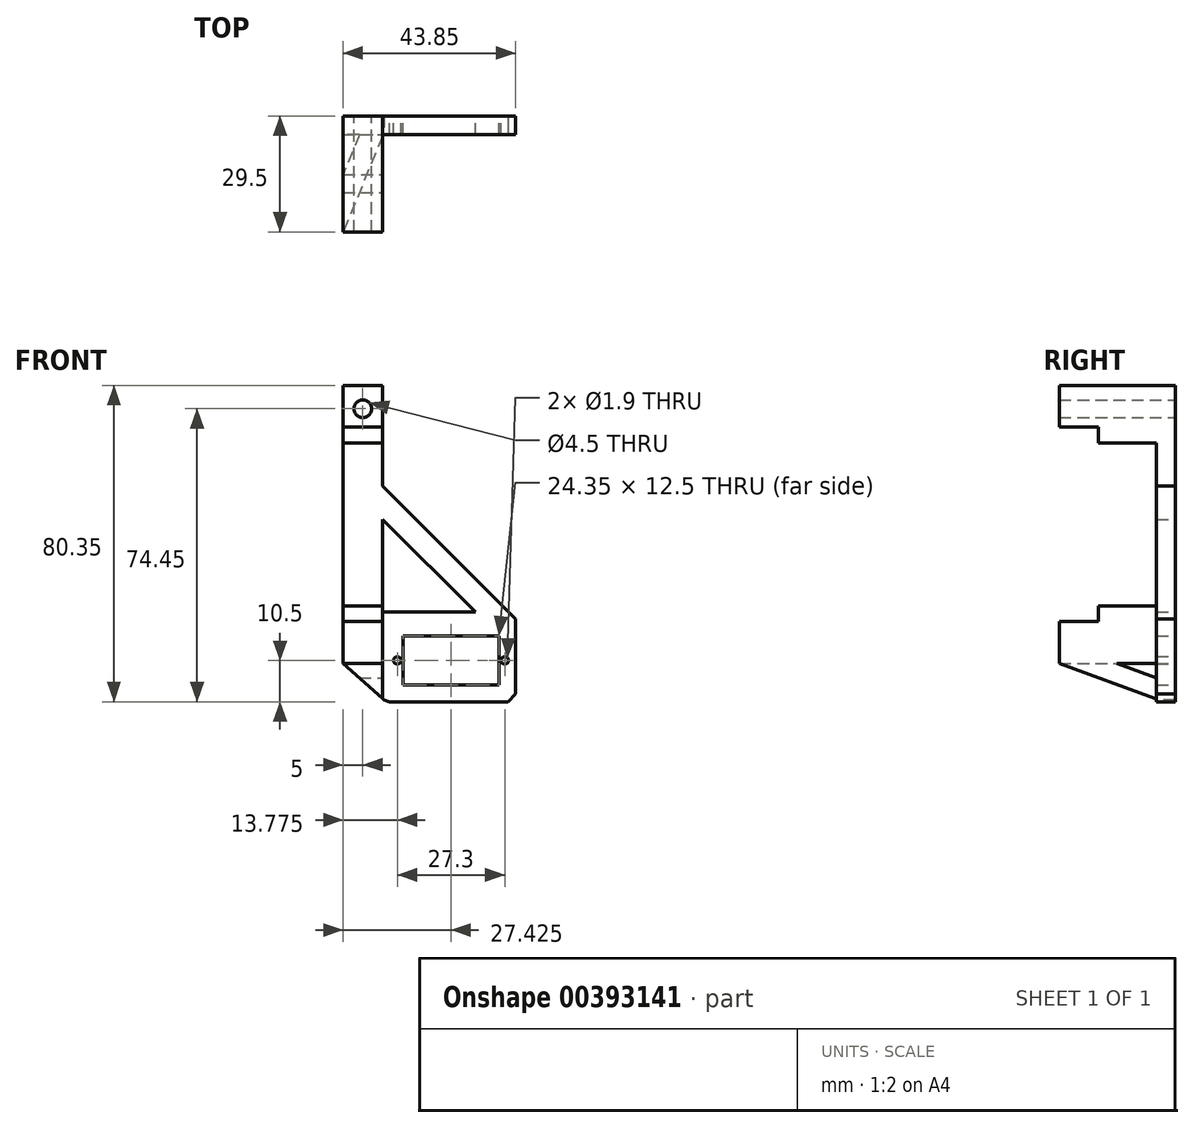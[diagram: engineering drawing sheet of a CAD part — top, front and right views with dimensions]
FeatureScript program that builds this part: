
annotation { "Feature Type Name" : "Feature", "Feature Type Description" : "" }
export const myFeature = defineFeature(function(context is Context, id is Id, definition is map)
    precondition{}
    {
        {
            var Q0;
            Q0=qCreatedBy(makeId("Front.planeOp"),FACE);
            var sketch = newSketch(context, id + "F0", { "sketchPlane" : qUnion([Q0])});
            skLineSegment(sketch, "E0", {"start": v(5, 35.3) * mm, "end": v(-5, 35.3) * mm});
            skPoint(sketch, "E1", {"position": v(0, 35.3) * mm});
            skLineSegment(sketch, "E2.MirrorCS", {"start": v(5, -35.3) * mm, "end": v(-5, -35.3) * mm});
            skPoint(sketch, "E3.MirrorP", {"position": v(0, -35.3) * mm});
            skLineSegment(sketch, "E4", {"start": v(-5, 35.3) * mm, "end": v(-5, -35.3) * mm});
            skLineSegment(sketch, "E5", {"start": v(5, -35.3) * mm, "end": v(5, 35.3) * mm});
            skLineSegment(sketch, "E6", {"start": v(-5, 24.7) * mm, "end": v(5, 24.7) * mm});
            skLineSegment(sketch, "E7", {"start": v(-5, 20.7) * mm, "end": v(5, 20.7) * mm});
            skLineSegment(sketch, "E8.MirrorCS", {"start": v(-5, -24.7) * mm, "end": v(5, -24.7) * mm});
            skLineSegment(sketch, "E9.MirrorCS", {"start": v(-5, -20.7) * mm, "end": v(5, -20.7) * mm});
            skCircle(sketch, "E10", {"center": v(0, 29.4) * mm, "radius": 2.25 * mm});
            skCircle(sketch, "E11.MirrorC", {"center": v(0, -29.4) * mm, "radius": 2.25 * mm});
            skLineSegment(sketch, "E12.bottom", {"start": v(10.25, -40.8) * mm, "end": v(34.6, -40.8) * mm});
            skLineSegment(sketch, "E12.top", {"start": v(10.25, -28.3) * mm, "end": v(34.6, -28.3) * mm});
            skLineSegment(sketch, "E12.left", {"start": v(10.25, -40.8) * mm, "end": v(10.25, -28.3) * mm});
            skLineSegment(sketch, "E12.right", {"start": v(34.6, -40.8) * mm, "end": v(34.6, -28.3) * mm});
            skPoint(sketch, "E12.middle", {"position": v(22.43, -34.55) * mm});
            skLineSegment(sketch, "E13.bottom", {"start": v(34.6, -28.3) * mm, "end": v(38.85, -28.3) * mm});
            skLineSegment(sketch, "E13.top", {"start": v(34.6, -40.8) * mm, "end": v(38.85, -40.8) * mm});
            skLineSegment(sketch, "E13.left", {"start": v(34.6, -28.3) * mm, "end": v(34.6, -40.8) * mm});
            skLineSegment(sketch, "E13.right", {"start": v(38.85, -28.3) * mm, "end": v(38.85, -40.8) * mm});
            skLineSegment(sketch, "E14.bottom", {"start": v(10.25, -28.3) * mm, "end": v(6, -28.3) * mm});
            skLineSegment(sketch, "E14.top", {"start": v(10.25, -40.8) * mm, "end": v(6, -40.8) * mm});
            skLineSegment(sketch, "E14.left", {"start": v(10.25, -28.3) * mm, "end": v(10.25, -40.8) * mm});
            skLineSegment(sketch, "E14.right", {"start": v(6, -28.3) * mm, "end": v(6, -40.8) * mm});
            skLineSegment(sketch, "E15.bottom", {"start": v(22.43, -28.3) * mm, "end": v(22.43, -28.3) * mm});
            skLineSegment(sketch, "E15.top", {"start": v(22.43, -40.8) * mm, "end": v(22.43, -40.8) * mm});
            skLineSegment(sketch, "E15.left", {"start": v(22.43, -28.3) * mm, "end": v(22.43, -40.8) * mm, "construction": true});
            skLineSegment(sketch, "E15.right", {"start": v(22.43, -28.3) * mm, "end": v(22.43, -40.8) * mm, "construction": true});
            skCircle(sketch, "E16", {"center": v(36.08, -34.55) * mm, "radius": 0.95 * mm});
            skPoint(sketch, "E16.centerSnap0", {"position": v(34.6, -34.55) * mm});
            skCircle(sketch, "E17.MirrorC", {"center": v(8.78, -34.55) * mm, "radius": 0.95 * mm});
            skLineSegment(sketch, "E18.bottom", {"start": v(38.85, -40.8) * mm, "end": v(6, -40.8) * mm});
            skLineSegment(sketch, "E18.top", {"start": v(38.85, -45.05) * mm, "end": v(6, -45.05) * mm});
            skLineSegment(sketch, "E18.left", {"start": v(38.85, -40.8) * mm, "end": v(38.85, -45.05) * mm});
            skLineSegment(sketch, "E18.right", {"start": v(6, -40.8) * mm, "end": v(6, -45.05) * mm});
            skLineSegment(sketch, "E19", {"start": v(34.6, -34.55) * mm, "end": v(10.25, -34.55) * mm, "construction": true});
            skLineSegment(sketch, "E20.MirrorCS", {"start": v(38.85, -28.3) * mm, "end": v(38.85, -24.05) * mm});
            skLineSegment(sketch, "E21.MirrorCS", {"start": v(38.85, -24.05) * mm, "end": v(6, -24.05) * mm});
            skLineSegment(sketch, "E22.MirrorCS", {"start": v(6, -28.3) * mm, "end": v(6, -24.05) * mm});
            skLineSegment(sketch, "E23", {"start": v(6, -45.05) * mm, "end": v(-5, -35.3) * mm});
            skLineSegment(sketch, "E24", {"start": v(38.85, -24.05) * mm, "end": v(5, 9.8) * mm});
            skLineSegment(sketch, "E25", {"start": v(6, -24.05) * mm, "end": v(5, -24.05) * mm});
            skLineSegment(sketch, "E26", {"start": v(28.61, -22.3) * mm, "end": v(5, 1.31) * mm});
            skLineSegment(sketch, "E27", {"start": v(5, 1.31) * mm, "end": v(28.61, -22.3) * mm});
            skLineSegment(sketch, "E28", {"start": v(28.61, -22.3) * mm, "end": v(5, -22.3) * mm});
            skSolve(sketch);
        }
        {
            var Q0;
            {var subQ0=sQuery(id+"F0.wireOp",EDGE,"E7");Q0=makeQuery(id+"F0.imprint","IMPRINT",FACE,{"disambiguationData":[TD([[makeQuery(id+"F0.imprint","IMPRINT",EDGE,{"derivedFrom":subQ0}),-1.0]])]});}
            extrude(context, id + "F1", {"entities" : qUnion([Q0]), "depth" : 4.8 * mm});
        }
        {
            var Q0;
            {var subQ0=sQuery(id+"F0.wireOp",EDGE,"E6");Q0=makeQuery(id+"F0.imprint","IMPRINT",FACE,{"disambiguationData":[TD([[makeQuery(id+"F0.imprint","IMPRINT",EDGE,{"derivedFrom":subQ0}),-1.0]])]});}
            var Q1;
            {var subQ0=sQuery(id+"F0.wireOp",EDGE,"E8.MirrorCS");Q1=makeQuery(id+"F0.imprint","IMPRINT",FACE,{"disambiguationData":[TD([[makeQuery(id+"F0.imprint","IMPRINT",EDGE,{"derivedFrom":subQ0}),1.0]])]});}
            extrude(context, id + "F2", {"entities" : qUnion([Q0, Q1]), "operationType" : NewBodyOperationType.ADD, "depth" : 19.5 * mm});
        }
        {
            var Q0;
            {var subQ1=sQuery(id+"F0.wireOp",EDGE,"E0");Q0=makeQuery(id+"F0.imprint","IMPRINT",FACE,{"disambiguationData":[TD([[makeQuery(id+"F0.imprint","IMPRINT",EDGE,{"derivedFrom":subQ1}),1.0]])]});}
            var Q1;
            Q1=makeQuery(id+"F0.imprint","IMPRINT",FACE,{"disambiguationData":[TD([[makeQuery(id+"F0.imprint","IMPRINT",EDGE,{"derivedFrom":sQuery(id+"F0.wireOp",EDGE,"E10")}),-1.0]])]});
            var Q2;
            {var subQ2=sQuery(id+"F0.wireOp",EDGE,"E2.MirrorCS");Q2=makeQuery(id+"F0.imprint","IMPRINT",FACE,{"disambiguationData":[TD([[makeQuery(id+"F0.imprint","IMPRINT",EDGE,{"derivedFrom":subQ2}),-1.0]])]});}
            var Q3;
            Q3=makeQuery(id+"F0.imprint","IMPRINT",FACE,{"disambiguationData":[TD([[makeQuery(id+"F0.imprint","IMPRINT",EDGE,{"derivedFrom":sQuery(id+"F0.wireOp",EDGE,"E11.MirrorC")}),1.0]])]});
            extrude(context, id + "F3", {"entities" : qUnion([Q0, Q1, Q2, Q3]), "operationType" : NewBodyOperationType.ADD, "depth" : 29.5 * mm});
        }
        {
            var Q0;
            {var subQ1=sQuery(id+"F0.wireOp",EDGE,"E2.MirrorCS");Q0=makeQuery(id+"F0.imprint","IMPRINT",FACE,{"disambiguationData":[TD([[makeQuery(id+"F0.imprint","IMPRINT",EDGE,{"derivedFrom":subQ1}),1.0]])]});}
            var Q1;
            Q1=makeQuery(id+"F0.imprint","IMPRINT",FACE,{"disambiguationData":[TD([[makeQuery(id+"F0.imprint","IMPRINT",EDGE,{"derivedFrom":sQuery(id+"F0.wireOp",EDGE,"E14.bottom")}),1.0]])]});
            var Q2;
            Q2=makeQuery(id+"F0.imprint","IMPRINT",FACE,{"disambiguationData":[TD([[makeQuery(id+"F0.imprint","IMPRINT",EDGE,{"derivedFrom":sQuery(id+"F0.wireOp",EDGE,"E18.top")}),-1.0]])]});
            var Q3;
            Q3=makeQuery(id+"F0.imprint","IMPRINT",FACE,{"disambiguationData":[TD([[makeQuery(id+"F0.imprint","IMPRINT",EDGE,{"derivedFrom":sQuery(id+"F0.wireOp",EDGE,"E13.bottom")}),-1.0]])]});
            var Q4;
            Q4=makeQuery(id+"F0.imprint","IMPRINT",FACE,{"disambiguationData":[TD([[makeQuery(id+"F0.imprint","IMPRINT",EDGE,{"derivedFrom":sQuery(id+"F0.wireOp",EDGE,"E12.top")}),1.0]])]});
            var Q5;
            Q5=makeQuery(id+"F0.imprint","IMPRINT",FACE,{"disambiguationData":[TD([[makeQuery(id+"F0.imprint","IMPRINT",EDGE,{"derivedFrom":sQuery(id+"F0.wireOp",EDGE,"E21.MirrorCS")}),-1.0]])]});
            var Q6;
            Q6=makeQuery(id+"F1.opExtrude","CAP_FACE",FACE,{"disambiguationData":[OSD([sQuery(id+"F0.wireOp",EDGE,"E4"),sQuery(id+"F0.wireOp",EDGE,"E5"),sQuery(id+"F0.wireOp",EDGE,"E7"),sQuery(id+"F0.wireOp",EDGE,"E9.MirrorCS")])],"isStart":false});
            extrude(context, id + "F4", {"entities" : qUnion([Q0, Q1, Q2, Q3, Q4, Q5]), "operationType" : NewBodyOperationType.ADD, "endBound" : BoundingType.UP_TO_SURFACE, "endBoundEntityFace" : qUnion([Q6]), "depth" : 25 * mm});
        }
        {
            var Q0;
            Q0=makeQuery(id+"F4.opExtrude","SWEPT_EDGE",EDGE,{"disambiguationData":[OSD([sQuery(id+"F0.wireOp",EDGE,"E18.top"),sQuery(id+"F0.wireOp",EDGE,"E18.left")])]});
            var Q1;
            Q1=makeQuery(id+"F4.opExtrude","SWEPT_EDGE",EDGE,{"disambiguationData":[OSD([sQuery(id+"F0.wireOp",EDGE,"E18.top"),sQuery(id+"F0.wireOp",EDGE,"E18.right"),sQuery(id+"F0.wireOp",EDGE,"E23")])]});
            chamfer(context, id + "F5", {"entities" : qUnion([Q0, Q1]), "width" : 2 * mm, "tangentPropagation" : true});
        }
        {
            var Q0;
            {var subQ1=sQuery(id+"F0.wireOp",EDGE,"E8.MirrorCS");var subQ2=sQuery(id+"F0.wireOp",EDGE,"E5");var subQ4=sQuery(id+"F0.wireOp",EDGE,"E2.MirrorCS");var subQ5=sQuery(id+"F0.wireOp",EDGE,"E9.MirrorCS");var subQ8=sQuery(id+"F0.wireOp",EDGE,"E6");var subQ9=sQuery(id+"F0.wireOp",EDGE,"E0");var subQ11=makeQuery(id+"F0.imprint","INTERSECT",VERTEX,{"derivedFrom":[subQ2,subQ8]});var subQ12=makeQuery(id+"F0.imprint","INTERSECT",VERTEX,{"derivedFrom":[subQ2,subQ1]});var subQ14=makeQuery(id+"F0.imprint","INTERSECT",VERTEX,{"derivedFrom":[subQ2,sQuery(id+"F0.wireOp",EDGE,"E25")]});Q0=makeQuery(id+"F4.boolean.opBoolean","SPLIT",FACE,{"disambiguationData":[TD([makeQuery(id+"F2.opExtrude","SWEPT_FACE",FACE,{"disambiguationData":[OSD([subQ5])]})])],"derivedFrom":makeQuery(id+"F3.boolean.opBoolean","MERGE",FACE,{"derivedFrom":[makeQuery(id+"F2.boolean.opBoolean","MERGE",FACE,{"derivedFrom":[makeQuery(id+"F1.opExtrude","SWEPT_FACE",FACE,{"disambiguationData":[OSD([subQ2])]}),makeQuery(id+"F2.opExtrude","SWEPT_FACE",FACE,{"disambiguationData":[OSD([subQ2]),TDD([makeQuery(id+"F0.imprint","IMPRINT",EDGE,{"disambiguationData":[TD([[subQ12,-1.0]])],"derivedFrom":subQ2})])]}),makeQuery(id+"F2.opExtrude","SWEPT_FACE",FACE,{"disambiguationData":[OSD([subQ2]),TDD([makeQuery(id+"F0.imprint","IMPRINT",EDGE,{"disambiguationData":[TD([[subQ11,1.0]])],"derivedFrom":subQ2})])]})]}),makeQuery(id+"F3.opExtrude","SWEPT_FACE",FACE,{"disambiguationData":[OSD([subQ2]),TDD([makeQuery(id+"F0.imprint","IMPRINT",EDGE,{"disambiguationData":[TD([[makeQuery(id+"F0.imprint","INTERSECT",VERTEX,{"derivedFrom":[subQ4,subQ2]}),-1.0]])],"derivedFrom":subQ2}),makeQuery(id+"F0.imprint","IMPRINT",EDGE,{"disambiguationData":[TD([[subQ14,-1.0]])],"derivedFrom":subQ2}),makeQuery(id+"F0.imprint","IMPRINT",EDGE,{"disambiguationData":[TD([[subQ12,1.0]])],"derivedFrom":subQ2})])]}),makeQuery(id+"F3.opExtrude","SWEPT_FACE",FACE,{"disambiguationData":[OSD([subQ2]),TDD([makeQuery(id+"F0.imprint","IMPRINT",EDGE,{"disambiguationData":[TD([[makeQuery(id+"F0.imprint","INTERSECT",VERTEX,{"derivedFrom":[subQ9,subQ2]}),1.0]])],"derivedFrom":subQ2})])]})]})});}
            var sketch = newSketch(context, id + "F6", { "sketchPlane" : qUnion([Q0])});
            skLineSegment(sketch, "E29", {"start": v(-4.8, -35.3) * mm, "end": v(-4.8, -44.3) * mm});
            skLineSegment(sketch, "E30", {"start": v(-4.8, -44.3) * mm, "end": v(-29.5, -35.3) * mm});
            skLineSegment(sketch, "E31", {"start": v(-29.5, -35.3) * mm, "end": v(-4.8, -35.3) * mm});
            skLineSegment(sketch, "E32", {"start": v(-4.8, -38.98) * mm, "end": v(-14.9, -35.3) * mm});
            skSolve(sketch);
        }
        {
            var Q0;
            {var subQ0=sQuery(id+"F6.wireOp",EDGE,"E30");Q0=makeQuery(id+"F6.imprint","IMPRINT",FACE,{"disambiguationData":[TD([[makeQuery(id+"F6.imprint","IMPRINT",EDGE,{"derivedFrom":subQ0}),-1.0]])]});}
            var Q1;
            Q1=makeQuery(id+"F4.opExtrude","SWEPT_FACE",FACE,{"disambiguationData":[OSD([sQuery(id+"F0.wireOp",EDGE,"E23")])]});
            extrude(context, id + "F7", {"entities" : qUnion([Q0]), "operationType" : NewBodyOperationType.ADD, "endBound" : BoundingType.UP_TO_SURFACE, "oppositeDirection" : true, "endBoundEntityFace" : qUnion([Q1]), "depth" : 25 * mm});
        }
    });
